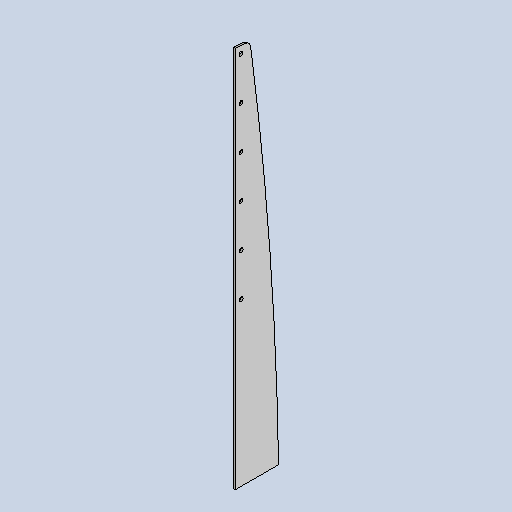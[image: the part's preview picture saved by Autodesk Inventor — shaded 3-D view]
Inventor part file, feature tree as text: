
AUTODESK INVENTOR PART (.ipt)
format: ipt  version: 2025 (Build 290162010, 162A)  size: 136,192 bytes
history: native  units: mm
features: sketch x2, other x2, sheet_metal_op x1, chamfer x1, extrude x1, pattern_linear x1
ambient origin geometry x8: Origin, YZ Plane, XZ Plane, XY Plane, X Axis, Y Axis, Z Axis, Center Point
bodies: Solid1 (feature_tree)
feature tree (8):
  sheet_metal_op  "Face1"
  chamfer  "Corner Round3"
  extrude  "Extrusion1"  Depth=5650.0mm
  pattern_linear  "Rectangular Pattern2"  Spacing1=14.870205mm  [1 undecoded]
  sketch  "Sketch1"  dims[d2=25.0mm d3=5650.0mm]
  other  "Plate1"
  sketch  "Sketch4"  dims[d4=3.0mm d7=14.870205mm d8=14.870205mm d9=10.0mm d23=7.0mm d25=10.0mm d26=0.0mm d27=0.0mm d29=60.0mm d31=72.5mm d32=13.0mm d33=97.0mm d34=651.812mm]
  other  "Definition1"
note: 1 required parameter value undecoded (feature->parameter linkage not recoverable at this tier; creation-order binding heuristic only, values carry confidence <= 0.55)
